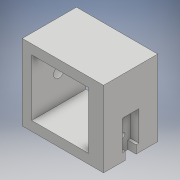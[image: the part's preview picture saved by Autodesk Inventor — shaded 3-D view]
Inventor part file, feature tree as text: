
AUTODESK INVENTOR PART (.ipt)
format: ipt  version: 2017 (Build 210142000, 142)  size: 137,728 bytes
history: native  units: mm
features: extrude x4, sketch x4
ambient origin geometry x8: Origin, YZ Plane, XZ Plane, XY Plane, X Axis, Y Axis, Z Axis, Center Point
bodies: Solid1 (feature_tree)
feature tree (8):
  extrude  "Extrusion1"  Depth=21.0mm
  extrude  "Extrusion2"  Depth=28.0mm
  extrude  "Extrusion3"  Depth=20.0mm
  extrude  "Extrusion4"  Depth=3.0mm
  sketch  "Sketch1"  dims[d0=21.0mm d1=21.0mm]
  sketch  "Sketch3"  dims[d2=28.0mm d3=28.0mm]
  sketch  "Sketch4"  dims[d4=20.0mm d5=0.0mm d6=2.0mm]
  sketch  "Sketch5"  dims[d7=3.0mm d8=3.0mm d9=1.0mm d10=3.0mm d11=1.0mm d12=3.0mm d13=0.0mm d14=1.9mm d15=1.9mm d16=6.0mm d17=3.0mm d18=0.0mm d19=3.9mm d20=4.0mm d21=0.0mm d22=2.5mm]
